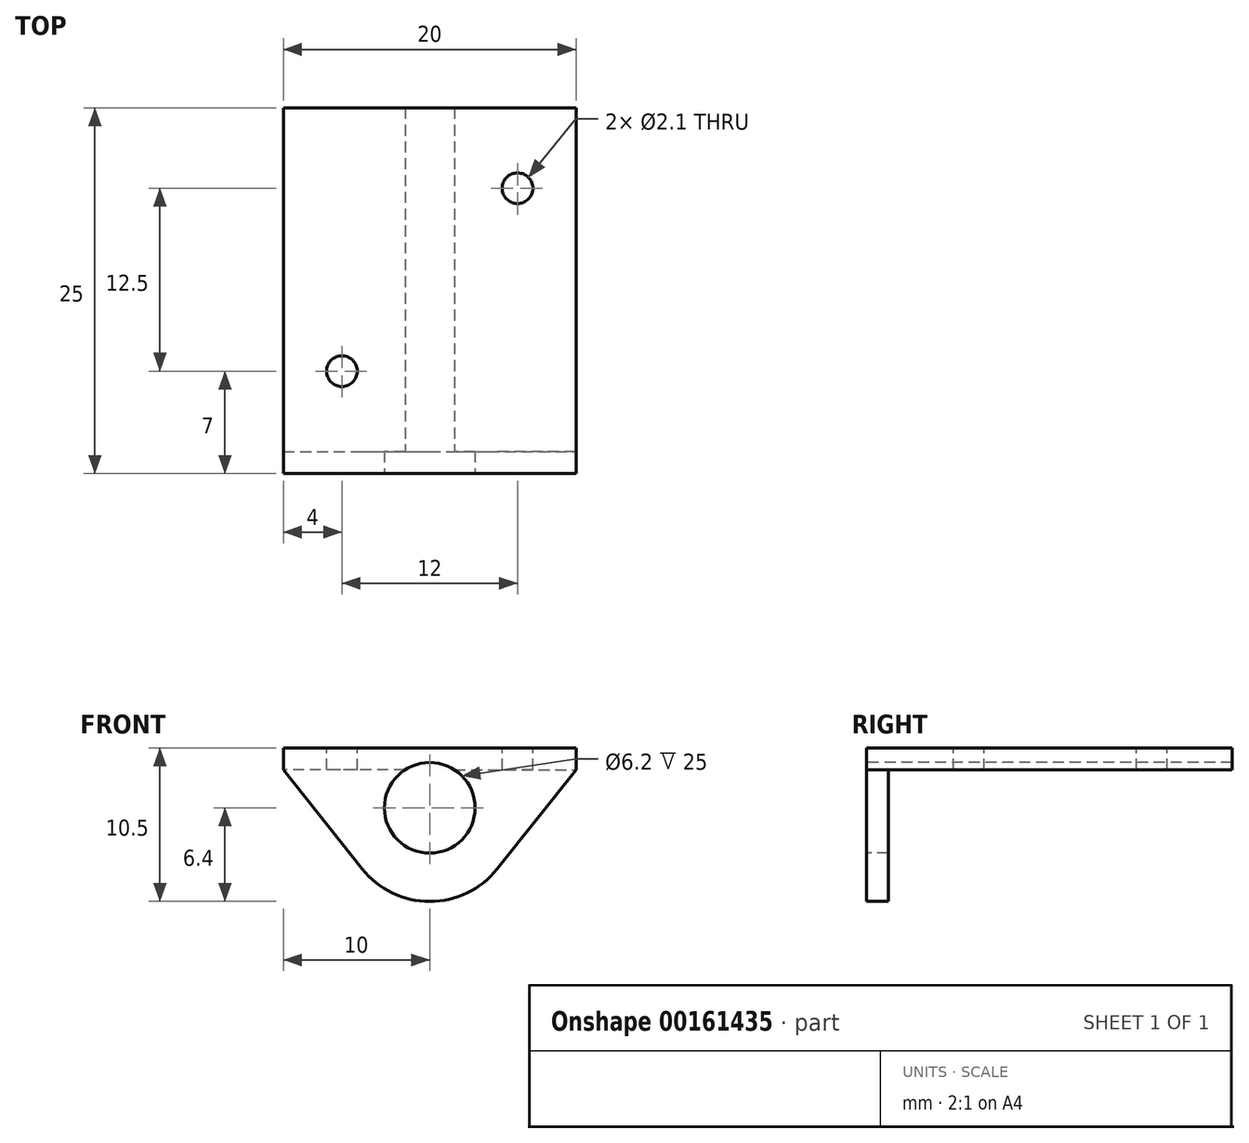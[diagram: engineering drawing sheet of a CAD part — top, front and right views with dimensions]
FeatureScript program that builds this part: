
annotation { "Feature Type Name" : "Feature", "Feature Type Description" : "" }
export const myFeature = defineFeature(function(context is Context, id is Id, definition is map)
    precondition{}
    {
        {
            var Q0;
            Q0=qCreatedBy(makeId("Top.planeOp"),FACE);
            var sketch = newSketch(context, id + "F0", { "sketchPlane" : qUnion([Q0])});
            skLineSegment(sketch, "E0.bottom", {"start": v(10, 12.5) * mm, "end": v(-10, 12.5) * mm});
            skLineSegment(sketch, "E0.top", {"start": v(10, -12.5) * mm, "end": v(-10, -12.5) * mm});
            skLineSegment(sketch, "E0.left", {"start": v(10, 12.5) * mm, "end": v(10, -12.5) * mm});
            skLineSegment(sketch, "E0.right", {"start": v(-10, 12.5) * mm, "end": v(-10, -12.5) * mm});
            skPoint(sketch, "E0.middle", {"position": v(0, 0) * mm});
            skCircle(sketch, "E1", {"center": v(6, 7) * mm, "radius": 1.05 * mm});
            skCircle(sketch, "E2", {"center": v(-6, -5.5) * mm, "radius": 1.05 * mm});
            skSolve(sketch);
        }
        {
            var Q0;
            Q0=makeQuery(id+"F0.imprint","IMPRINT",FACE,{"disambiguationData":[TD([[makeQuery(id+"F0.imprint","IMPRINT",EDGE,{"derivedFrom":sQuery(id+"F0.wireOp",EDGE,"E0.bottom")}),1.0]])]});
            extrude(context, id + "F1", {"entities" : qUnion([Q0]), "oppositeDirection" : true, "depth" : 1.5 * mm});
        }
        {
            var Q0;
            Q0=makeQuery(id+"F1.opExtrude","CAP_FACE",FACE,{"disambiguationData":[OSD([sQuery(id+"F0.wireOp",EDGE,"E0.bottom"),sQuery(id+"F0.wireOp",EDGE,"E0.top"),sQuery(id+"F0.wireOp",EDGE,"E0.left"),sQuery(id+"F0.wireOp",EDGE,"E0.right")])],"isStart":false});
            var sketch = newSketch(context, id + "F2", { "sketchPlane" : qUnion([Q0])});
            skLineSegment(sketch, "E3.bottom", {"start": v(-10, 12.5) * mm, "end": v(10, 12.5) * mm});
            skLineSegment(sketch, "E3.top", {"start": v(-10, 11) * mm, "end": v(10, 11) * mm});
            skLineSegment(sketch, "E3.left", {"start": v(-10, 12.5) * mm, "end": v(-10, 11) * mm});
            skLineSegment(sketch, "E3.right", {"start": v(10, 12.5) * mm, "end": v(10, 11) * mm});
            skSolve(sketch);
        }
        {
            var Q0;
            Q0=qSketchRegion(id+"F2",true);
            extrude(context, id + "F3", {"entities" : qUnion([Q0]), "operationType" : NewBodyOperationType.ADD, "depth" : 9 * mm});
        }
        {
            var Q0;
            Q0=makeQuery(id+"F3.boolean.opBoolean","MERGE",FACE,{"derivedFrom":[makeQuery(id+"F1.opExtrude","SWEPT_FACE",FACE,{"disambiguationData":[OSD([sQuery(id+"F0.wireOp",EDGE,"E0.top")])]}),makeQuery(id+"F3.opExtrude","SWEPT_FACE",FACE,{"disambiguationData":[OSD([sQuery(id+"F2.wireOp",EDGE,"E3.bottom")])]})]});
            var sketch = newSketch(context, id + "F4", { "sketchPlane" : qUnion([Q0])});
            skCircle(sketch, "E4", {"center": v(0, -4.1) * mm, "radius": 3.1 * mm});
            skLineSegment(sketch, "E5", {"start": v(-10, -1.5) * mm, "end": v(-4.62, -8.27) * mm});
            skLineSegment(sketch, "E6", {"start": v(10, -1.5) * mm, "end": v(4.62, -8.27) * mm});
            skArc(sketch, "E7.trimOffspring", {"start": v(-4.62, -8.27) * mm, "mid": v(0, -10.5) * mm, "end": v(4.62, -8.27) * mm});
            skSolve(sketch);
        }
        {
            var Q0;
            Q0=qSketchRegion(id+"F4",true);
            var Q1;
            {var subQ0=sQuery(id+"F4.wireOp",EDGE,"E5");Q1=makeQuery(id+"F4.imprint","IMPRINT",FACE,{"disambiguationData":[TD([[makeQuery(id+"F4.imprint","IMPRINT",EDGE,{"derivedFrom":subQ0}),-1.0]])]});}
            var Q2;
            {var subQ0=sQuery(id+"F4.wireOp",EDGE,"E6");Q2=makeQuery(id+"F4.imprint","IMPRINT",FACE,{"disambiguationData":[TD([[makeQuery(id+"F4.imprint","IMPRINT",EDGE,{"derivedFrom":subQ0}),1.0]])]});}
            extrude(context, id + "F5", {"entities" : qUnion([Q0, Q1, Q2]), "operationType" : NewBodyOperationType.REMOVE, "oppositeDirection" : true, "depth" : 30 * mm});
        }
    });
